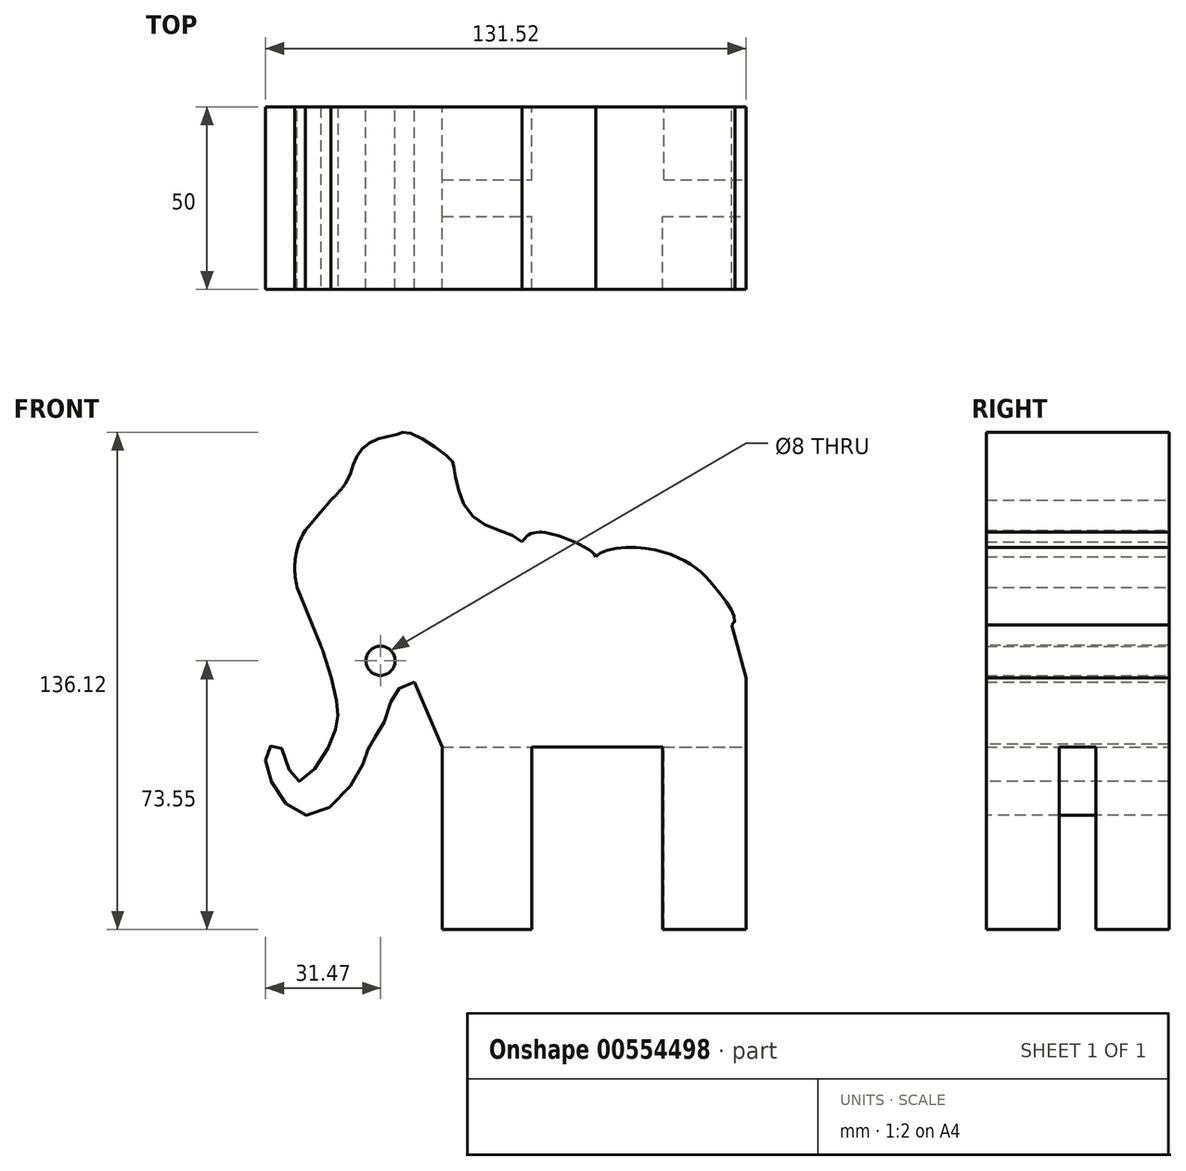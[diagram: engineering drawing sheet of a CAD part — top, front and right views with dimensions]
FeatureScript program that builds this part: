
annotation { "Feature Type Name" : "Feature", "Feature Type Description" : "" }
export const myFeature = defineFeature(function(context is Context, id is Id, definition is map)
    precondition{}
    {
        {
            var Q0;
            Q0=qCreatedBy(makeId("Front.planeOp"),FACE);
            var sketch = newSketch(context, id + "F0", { "sketchPlane" : qUnion([Q0])});
            skLineSegment(sketch, "E0", {"start": v(54.75, -3.75) * mm, "end": v(58.65, -18.15) * mm});
            skLineSegment(sketch, "E1", {"start": v(58.65, -18.15) * mm, "end": v(58.65, -37.05) * mm});
            skLineSegment(sketch, "E2", {"start": v(58.65, -37.05) * mm, "end": v(-24.45, -37.05) * mm});
            skLineSegment(sketch, "E3", {"start": v(-24.45, -37.05) * mm, "end": v(-32.55, -18.15) * mm});
            skLineSegment(sketch, "E4", {"start": v(-32.55, -18.15) * mm, "end": v(-5.55, 9.45) * mm});
            skFitSpline(sketch, "E5", {"points": [v(17.55, 13.35) * mm, v(9.88, 19.76) * mm, v(0, 21.37) * mm, v(-3.06, 18.32) * mm, v(-5.55, 13.35) * mm, v(-5.55, 9.45) * mm, v(17.55, 13.35) * mm]});
            skFitSpline(sketch, "E6", {"points": [v(17.55, 13.35) * mm, v(27.34, 17.54) * mm, v(42.8, 13.35) * mm, v(50.59, 6.14) * mm, v(54.75, -3.75) * mm, v(17.55, 13.35) * mm]});
            skSolve(sketch);
        }
        {
            var Q0;
            Q0 = qSketchRegion(id + "F0", true);
            extrude(context, id + "F1", {"entities" : qUnion([Q0]), "depth" : 50 * mm, "offsetDistance" : 25 * mm});
        }
        {
            var Q0;
            Q0=makeQuery(id+"F1.opExtrude","SWEPT_FACE",FACE,{"disambiguationData":[OSD([sQuery(id+"F0.wireOp",EDGE,"E2")])]});
            var sketch = newSketch(context, id + "F2", { "sketchPlane" : qUnion([Q0])});
            skLineSegment(sketch, "E7.bottom", {"start": v(35.78, 50) * mm, "end": v(58.65, 50) * mm});
            skLineSegment(sketch, "E7.top", {"start": v(35.78, 30) * mm, "end": v(58.65, 30) * mm});
            skLineSegment(sketch, "E7.left", {"start": v(35.78, 50) * mm, "end": v(35.78, 30) * mm});
            skLineSegment(sketch, "E7.right", {"start": v(58.65, 50) * mm, "end": v(58.65, 30) * mm});
            skLineSegment(sketch, "E8.bottom", {"start": v(36.16, 20) * mm, "end": v(58.65, 20) * mm});
            skLineSegment(sketch, "E8.top", {"start": v(36.16, 0) * mm, "end": v(58.65, 0) * mm});
            skLineSegment(sketch, "E8.left", {"start": v(36.16, 20) * mm, "end": v(36.16, 0) * mm});
            skLineSegment(sketch, "E8.right", {"start": v(58.65, 20) * mm, "end": v(58.65, 0) * mm});
            skLineSegment(sketch, "E9.bottom", {"start": v(-24.45, 50) * mm, "end": v(0, 50) * mm});
            skLineSegment(sketch, "E9.top", {"start": v(-24.45, 30) * mm, "end": v(0, 30) * mm});
            skLineSegment(sketch, "E9.left", {"start": v(-24.45, 50) * mm, "end": v(-24.45, 30) * mm});
            skLineSegment(sketch, "E9.right", {"start": v(0, 50) * mm, "end": v(0, 30) * mm});
            skLineSegment(sketch, "E10.bottom", {"start": v(-24.45, 20) * mm, "end": v(0, 20) * mm});
            skLineSegment(sketch, "E10.top", {"start": v(-24.45, 0) * mm, "end": v(0, 0) * mm});
            skLineSegment(sketch, "E10.left", {"start": v(-24.45, 20) * mm, "end": v(-24.45, 0) * mm});
            skLineSegment(sketch, "E10.right", {"start": v(0, 20) * mm, "end": v(0, 0) * mm});
            skSolve(sketch);
        }
        {
            var Q0;
            Q0=makeQuery(id+"F2.imprint","IMPRINT",FACE,{"disambiguationData":[TD([[makeQuery(id+"F2.imprint","IMPRINT",EDGE,{"derivedFrom":sQuery(id+"F2.wireOp",EDGE,"E8.bottom")}),-1.0]])]});
            var Q1;
            Q1=makeQuery(id+"F2.imprint","IMPRINT",FACE,{"disambiguationData":[TD([[makeQuery(id+"F2.imprint","IMPRINT",EDGE,{"derivedFrom":sQuery(id+"F2.wireOp",EDGE,"E7.bottom")}),1.0]])]});
            var Q2;
            Q2=makeQuery(id+"F2.imprint","IMPRINT",FACE,{"disambiguationData":[TD([[makeQuery(id+"F2.imprint","IMPRINT",EDGE,{"derivedFrom":sQuery(id+"F2.wireOp",EDGE,"E10.bottom")}),-1.0]])]});
            var Q3;
            Q3=makeQuery(id+"F2.imprint","IMPRINT",FACE,{"disambiguationData":[TD([[makeQuery(id+"F2.imprint","IMPRINT",EDGE,{"derivedFrom":sQuery(id+"F2.wireOp",EDGE,"E9.bottom")}),1.0]])]});
            extrude(context, id + "F3", {"entities" : qUnion([Q0, Q1, Q2, Q3]), "operationType" : NewBodyOperationType.ADD, "depth" : 50 * mm, "offsetDistance" : 25 * mm});
        }
        {
            var Q0;
            Q0=qCreatedBy(makeId("Front.planeOp"),FACE);
            var sketch = newSketch(context, id + "F4", { "sketchPlane" : qUnion([Q0])});
            skLineSegment(sketch, "E11", {"start": v(-57.12, -10.97) * mm, "end": v(-64.26, 6.64) * mm});
            skLineSegment(sketch, "E12", {"start": v(-62.01, 22.26) * mm, "end": v(-51.03, 34.96) * mm});
            skFitSpline(sketch, "E13", {"points": [v(-57.12, -10.97) * mm, v(-53.24, -25.82) * mm, v(-53.27, -30.55) * mm, v(-57.12, -39.8) * mm, v(-64.63, -46.3) * mm, v(-68.96, -36.88) * mm, v(-72.1, -37.47) * mm, v(-71.2, -46.85) * mm, v(-60.3, -55.71) * mm, v(-46.75, -43.06) * mm, v(-44.47, -36.87) * mm, v(-40.92, -31.4) * mm, v(-37.35, -22.14) * mm, v(-30.8, -18.75) * mm, v(-3.6, 0) * mm, v(0, 11.98) * mm, v(-3.18, 19.52) * mm, v(-16.61, 26.54) * mm, v(-21.24, 39.4) * mm, v(-22.17, 41.59) * mm, v(-33.45, 48.9) * mm, v(-37.35, 48.33) * mm, v(-43.76, 46.51) * mm, v(-48.17, 41.88) * mm, v(-51.03, 34.96) * mm, v(-62.01, 22.26) * mm, v(-64.26, 6.64) * mm, v(-57.12, -10.97) * mm]});
            skSolve(sketch);
        }
        {
            var Q0;
            {var subQ0=sQuery(id+"F4.wireOp",EDGE,"E13");var subQ4=sQuery(id+"F4.wireOp",EDGE,"E11");var subQ7=makeQuery(id+"F4.imprint","INTERSECT",VERTEX,{"disambiguationData":[OD(1.0)],"derivedFrom":[subQ4,subQ0]});Q0=makeQuery(id+"F4.imprint","IMPRINT",FACE,{"disambiguationData":[TD([[makeQuery(id+"F4.imprint","IMPRINT",EDGE,{"disambiguationData":[TD([[subQ7,1.0]])],"derivedFrom":subQ4}),-1.0]])]});}
            extrude(context, id + "F5", {"entities" : qUnion([Q0]), "operationType" : NewBodyOperationType.ADD, "depth" : 50 * mm, "offsetDistance" : 25 * mm});
        }
        {
            var Q0;
            Q0=qCreatedBy(makeId("Front.planeOp"),FACE);
            var sketch = newSketch(context, id + "F6", { "sketchPlane" : qUnion([Q0])});
            skCircle(sketch, "E14", {"center": v(-41.4, -13.5) * mm, "radius": 4 * mm});
            skSolve(sketch);
        }
        {
            var Q0;
            Q0 = qSketchRegion(id + "F6", true);
            extrude(context, id + "F7", {"entities" : qUnion([Q0]), "operationType" : NewBodyOperationType.REMOVE, "endBound" : BoundingType.THROUGH_ALL, "depth" : 60 * mm, "offsetDistance" : 25 * mm});
        }
    });
